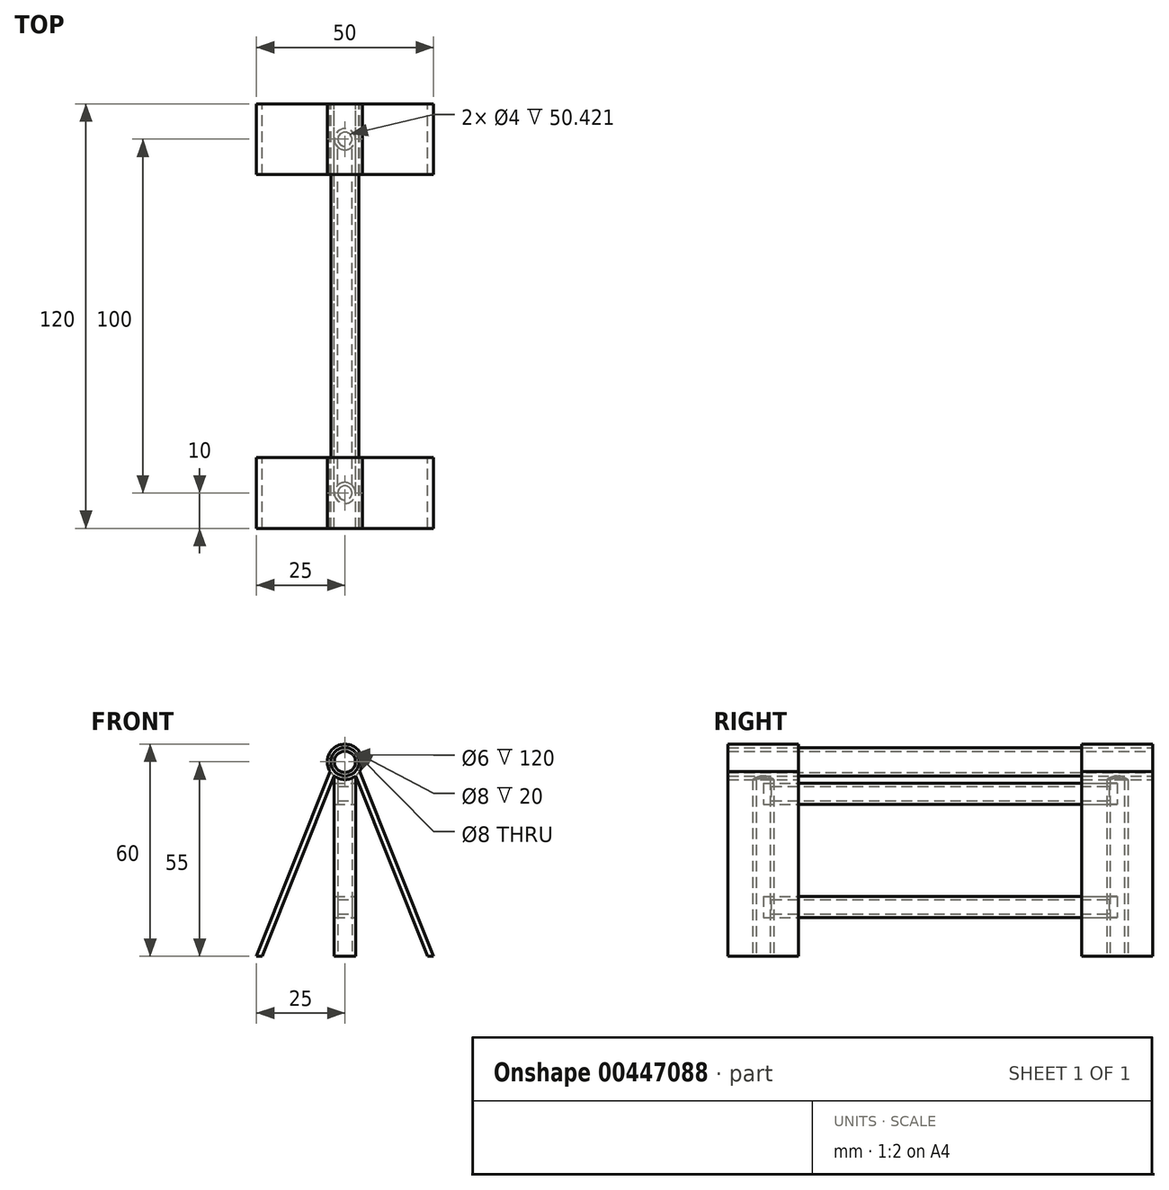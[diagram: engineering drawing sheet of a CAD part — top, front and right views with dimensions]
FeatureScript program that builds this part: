
annotation { "Feature Type Name" : "Feature", "Feature Type Description" : "" }
export const myFeature = defineFeature(function(context is Context, id is Id, definition is map)
    precondition{}
    {
        {
            var Q0;
            Q0=qCreatedBy(makeId("Top.planeOp"),FACE);
            var sketch = newSketch(context, id + "F0", { "sketchPlane" : qUnion([Q0])});
            skCircle(sketch, "E0", {"center": v(0, -10) * mm, "radius": 3 * mm});
            skCircle(sketch, "E1", {"center": v(0, -110) * mm, "radius": 3 * mm});
            skCircle(sketch, "E2", {"center": v(0, -10) * mm, "radius": 2 * mm});
            skCircle(sketch, "E3", {"center": v(0, -110) * mm, "radius": 2 * mm});
            skSolve(sketch);
        }
        {
            var Q0;
            Q0=qCreatedBy(makeId("Front.planeOp"),FACE);
            var sketch = newSketch(context, id + "F1", { "sketchPlane" : qUnion([Q0])});
            skCircle(sketch, "E4", {"center": v(0, 55) * mm, "radius": 4 * mm});
            skCircle(sketch, "E5", {"center": v(0, 55) * mm, "radius": 5 * mm});
            skLineSegment(sketch, "E6", {"start": v(-25, 0) * mm, "end": v(25, 0) * mm, "construction": true});
            skLineSegment(sketch, "E7", {"start": v(-4.14, 52.2) * mm, "end": v(-25, 0) * mm});
            skLineSegment(sketch, "E8", {"start": v(-3, 51) * mm, "end": v(-23.38, 0) * mm});
            skLineSegment(sketch, "E9", {"start": v(-13.2, 25.5) * mm, "end": v(-14.59, 26.06) * mm, "construction": true});
            skLineSegment(sketch, "E10", {"start": v(25, 0) * mm, "end": v(4.14, 52.2) * mm});
            skLineSegment(sketch, "E11", {"start": v(3, 51) * mm, "end": v(23.38, 0) * mm});
            skLineSegment(sketch, "E12", {"start": v(13.2, 25.5) * mm, "end": v(14.59, 26.06) * mm, "construction": true});
            skLineSegment(sketch, "E13", {"start": v(-25, 0) * mm, "end": v(-23.38, 0) * mm});
            skLineSegment(sketch, "E14", {"start": v(23.38, 0) * mm, "end": v(25, 0) * mm});
            skLineSegment(sketch, "E15.bottom", {"start": v(-3, 49) * mm, "end": v(3, 49) * mm});
            skLineSegment(sketch, "E15.top", {"start": v(-3, 43) * mm, "end": v(3, 43) * mm});
            skLineSegment(sketch, "E15.left", {"start": v(-3, 49) * mm, "end": v(-3, 43) * mm});
            skLineSegment(sketch, "E15.right", {"start": v(3, 49) * mm, "end": v(3, 43) * mm});
            skLineSegment(sketch, "E16.bottom", {"start": v(-2, 48) * mm, "end": v(2, 48) * mm});
            skLineSegment(sketch, "E16.top", {"start": v(-2, 44) * mm, "end": v(2, 44) * mm});
            skLineSegment(sketch, "E16.left", {"start": v(-2, 48) * mm, "end": v(-2, 44) * mm});
            skLineSegment(sketch, "E16.right", {"start": v(2, 48) * mm, "end": v(2, 44) * mm});
            skLineSegment(sketch, "E17", {"start": v(2, 44) * mm, "end": v(3, 44) * mm, "construction": true});
            skLineSegment(sketch, "E18", {"start": v(2, 44) * mm, "end": v(2, 43) * mm, "construction": true});
            skPoint(sketch, "E19", {"position": v(0, 46) * mm});
            skLineSegment(sketch, "E20.bottom", {"start": v(-3, 17) * mm, "end": v(3, 17) * mm});
            skLineSegment(sketch, "E20.top", {"start": v(-3, 11) * mm, "end": v(3, 11) * mm});
            skLineSegment(sketch, "E20.left", {"start": v(-3, 17) * mm, "end": v(-3, 11) * mm});
            skLineSegment(sketch, "E20.right", {"start": v(3, 17) * mm, "end": v(3, 11) * mm});
            skLineSegment(sketch, "E21.bottom", {"start": v(-2, 16) * mm, "end": v(2, 16) * mm});
            skLineSegment(sketch, "E21.top", {"start": v(-2, 12) * mm, "end": v(2, 12) * mm});
            skLineSegment(sketch, "E21.left", {"start": v(-2, 16) * mm, "end": v(-2, 12) * mm});
            skLineSegment(sketch, "E21.right", {"start": v(2, 16) * mm, "end": v(2, 12) * mm});
            skLineSegment(sketch, "E22", {"start": v(2, 12) * mm, "end": v(3, 12) * mm, "construction": true});
            skLineSegment(sketch, "E23", {"start": v(2, 12) * mm, "end": v(2, 11) * mm, "construction": true});
            skPoint(sketch, "E24", {"position": v(0, 14) * mm});
            skLineSegment(sketch, "E25", {"start": v(3, 51) * mm, "end": v(3, 0) * mm, "construction": true});
            skLineSegment(sketch, "E26", {"start": v(-3, 51) * mm, "end": v(-3, 0) * mm, "construction": true});
            skCircle(sketch, "E27", {"center": v(0, 55) * mm, "radius": 3 * mm});
            skSolve(sketch);
        }
        {
            var Q0;
            {var subQ0=sQuery(id+"F1.wireOp",EDGE,"E7");Q0=makeQuery(id+"F1.imprint","IMPRINT",FACE,{"disambiguationData":[TD([[makeQuery(id+"F1.imprint","IMPRINT",EDGE,{"derivedFrom":subQ0}),1.0]])]});}
            var Q1;
            {var subQ0=sQuery(id+"F1.wireOp",EDGE,"E10");Q1=makeQuery(id+"F1.imprint","IMPRINT",FACE,{"disambiguationData":[TD([[makeQuery(id+"F1.imprint","IMPRINT",EDGE,{"derivedFrom":subQ0}),1.0]])]});}
            extrude(context, id + "F2", {"entities" : qUnion([Q0, Q1]), "depth" : 20 * mm});
        }
        {
            var Q0;
            Q0=makeQuery(id+"F1.imprint","IMPRINT",FACE,{"disambiguationData":[TD([[makeQuery(id+"F1.imprint","IMPRINT",EDGE,{"derivedFrom":sQuery(id+"F1.wireOp",EDGE,"E15.bottom")}),-1.0]])]});
            var Q1;
            Q1=makeQuery(id+"F1.imprint","IMPRINT",FACE,{"disambiguationData":[TD([[makeQuery(id+"F1.imprint","IMPRINT",EDGE,{"derivedFrom":sQuery(id+"F1.wireOp",EDGE,"E20.bottom")}),-1.0]])]});
            extrude(context, id + "F3", {"entities" : qUnion([Q0, Q1]), "depth" : 110 * mm, "hasSecondDirection" : true, "secondDirectionOppositeDirection" : false, "secondDirectionDepth" : 10 * mm});
        }
        {
            var Q0;
            Q0=makeQuery(id+"F0.imprint","IMPRINT",FACE,{"disambiguationData":[TD([[makeQuery(id+"F0.imprint","IMPRINT",EDGE,{"derivedFrom":sQuery(id+"F0.wireOp",EDGE,"E2")}),1.0]])]});
            var Q1;
            Q1=makeQuery(id+"F0.imprint","IMPRINT",FACE,{"disambiguationData":[TD([[makeQuery(id+"F0.imprint","IMPRINT",EDGE,{"derivedFrom":sQuery(id+"F0.wireOp",EDGE,"E0")}),1.0]])]});
            var Q2;
            Q2=makeQuery(id+"F0.imprint","IMPRINT",FACE,{"disambiguationData":[TD([[makeQuery(id+"F0.imprint","IMPRINT",EDGE,{"derivedFrom":sQuery(id+"F0.wireOp",EDGE,"E1")}),1.0]])]});
            var Q3;
            Q3=makeQuery(id+"F0.imprint","IMPRINT",FACE,{"disambiguationData":[TD([[makeQuery(id+"F0.imprint","IMPRINT",EDGE,{"derivedFrom":sQuery(id+"F0.wireOp",EDGE,"E3")}),1.0]])]});
            extrude(context, id + "F4", {"entities" : qUnion([Q0, Q1, Q2, Q3]), "operationType" : NewBodyOperationType.REMOVE, "depth" : 50 * mm});
        }
        {
            var Q0;
            Q0 = qSketchRegion(id + "F0", true);
            extrude(context, id + "F5", {"entities" : qUnion([Q0]), "depth" : 55 * mm});
        }
        {
            var Q0;
            Q0=makeQuery(id+"F1.imprint","IMPRINT",FACE,{"disambiguationData":[TD([[makeQuery(id+"F1.imprint","IMPRINT",EDGE,{"derivedFrom":sQuery(id+"F1.wireOp",EDGE,"E4")}),1.0]])]});
            var Q1;
            Q1=makeQuery(id+"F1.imprint","IMPRINT",FACE,{"disambiguationData":[TD([[makeQuery(id+"F1.imprint","IMPRINT",EDGE,{"derivedFrom":sQuery(id+"F1.wireOp",EDGE,"E4")}),-1.0]])]});
            var Q2;
            Q2=makeQuery(id+"F1.imprint","IMPRINT",FACE,{"disambiguationData":[TD([[makeQuery(id+"F1.imprint","IMPRINT",EDGE,{"derivedFrom":sQuery(id+"F1.wireOp",EDGE,"E27")}),1.0]])]});
            extrude(context, id + "F6", {"entities" : qUnion([Q0, Q1, Q2]), "operationType" : NewBodyOperationType.REMOVE, "depth" : 120 * mm});
        }
        {
            var Q0;
            Q0=makeQuery(id+"F1.imprint","IMPRINT",FACE,{"disambiguationData":[TD([[makeQuery(id+"F1.imprint","IMPRINT",EDGE,{"derivedFrom":sQuery(id+"F1.wireOp",EDGE,"E4")}),-1.0]])]});
            extrude(context, id + "F7", {"entities" : qUnion([Q0]), "depth" : 20 * mm});
        }
        {
            var Q0;
            Q0=makeQuery(id+"F1.imprint","IMPRINT",FACE,{"disambiguationData":[TD([[makeQuery(id+"F1.imprint","IMPRINT",EDGE,{"derivedFrom":sQuery(id+"F1.wireOp",EDGE,"E4")}),-1.0]])]});
            var Q1;
            {var subQ0=sQuery(id+"F1.wireOp",EDGE,"E7");Q1=makeQuery(id+"F1.imprint","IMPRINT",FACE,{"disambiguationData":[TD([[makeQuery(id+"F1.imprint","IMPRINT",EDGE,{"derivedFrom":subQ0}),1.0]])]});}
            var Q2;
            {var subQ0=sQuery(id+"F1.wireOp",EDGE,"E10");Q2=makeQuery(id+"F1.imprint","IMPRINT",FACE,{"disambiguationData":[TD([[makeQuery(id+"F1.imprint","IMPRINT",EDGE,{"derivedFrom":subQ0}),1.0]])]});}
            extrude(context, id + "F8", {"entities" : qUnion([Q0, Q1, Q2]), "depth" : 120 * mm, "hasSecondDirection" : true, "secondDirectionOppositeDirection" : false, "secondDirectionDepth" : 100 * mm});
        }
        {
            var Q0;
            Q0=makeQuery(id+"F1.imprint","IMPRINT",FACE,{"disambiguationData":[TD([[makeQuery(id+"F1.imprint","IMPRINT",EDGE,{"derivedFrom":sQuery(id+"F1.wireOp",EDGE,"E4")}),1.0]])]});
            extrude(context, id + "F9", {"entities" : qUnion([Q0]), "depth" : 120 * mm});
        }
    });
